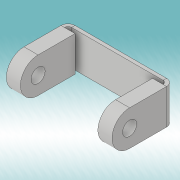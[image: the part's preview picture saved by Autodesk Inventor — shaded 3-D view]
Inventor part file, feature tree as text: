
AUTODESK INVENTOR PART (.ipt)
format: ipt  version: 2019 (Build 230136000, 136)  size: 195,584 bytes
history: native  units: in
note: dims shown in document units (in); Inventor stores cm internally (conversion verified against a paired STEP export)
features: sketch x8, sheet_metal_op x6, other x4, extrude x3
ambient origin geometry x8: Origin, YZ Plane, XZ Plane, XY Plane, X Axis, Y Axis, Z Axis, Center Point
bodies: Solid1 (feature_tree)
feature tree (21):
  extrude  "Extrusion1"  Depth=0.0787in TaperAngle=0.0deg
  sheet_metal_op  "Flange1"
  sheet_metal_op  "Flange2"
  extrude  "Extrusion3"  Depth=0.0787in
  extrude  "Extrusion4"  Depth=0.0787in
  sketch  "Sketch10"  dims[d16=0.0787in d17=0.0787in d18=0.0787in d19=0.0394in d20=0.1575in d21=0.0787in d22=1.378in d23=90.0deg d24=0.0787in d25=0.315in d26=0.0787in d27=0.0787in d38=0.3937in d39=0.3937in d40=0.3937in d41=0.0787in d42=0.0in d43=0.3937in d44=0.0787in d45=0.0in d46=0.315in d47=0.315in d54=0.315in d55=0.0in d56=0.2362in d57=0.0in]
  sketch  "Sketch1"  dims[d0=1.1811in d4=0.0787in d5=0.0in]
  sketch  "Sketch2"  dims[d6=0.7874in d7=0.0787in]
  other  "Plate1"
  sheet_metal_op  "Bend1"
  sheet_metal_op  "Corner1"
  sketch  "Sketch3"  dims[d8=0.0787in d9=0.0394in]
  other  "Plate2"
  sheet_metal_op  "Bend2"
  sheet_metal_op  "Corner2"
  sketch  "Sketch5"  dims[d10=0.1575in]
  sketch  "Sketch6"  dims[d11=0.0787in]
  sketch  "Sketch8"  dims[d12=1.378in d13=90.0deg d14=0.0787in]
  sketch  "Sketch9"  dims[d15=0.315in]
  other  "Cut1"
  other  "Cut2"
